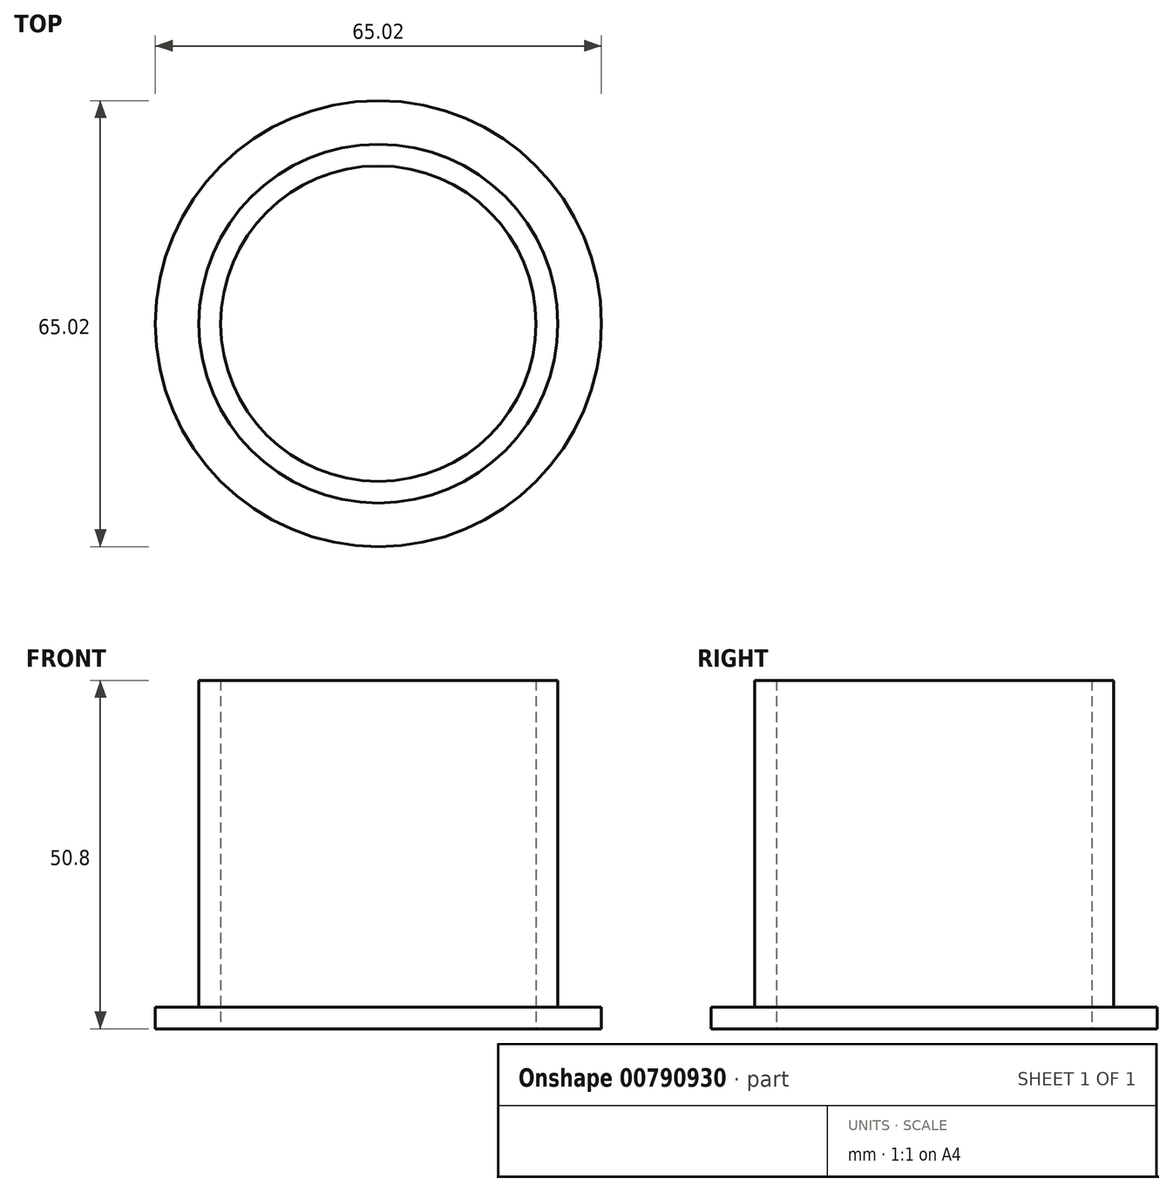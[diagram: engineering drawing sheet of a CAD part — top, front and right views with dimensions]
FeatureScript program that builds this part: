
annotation { "Feature Type Name" : "Feature", "Feature Type Description" : "" }
export const myFeature = defineFeature(function(context is Context, id is Id, definition is map)
    precondition{}
    {
        {
            var Q0;
            Q0=qCreatedBy(makeId("Front.planeOp"),FACE);
            var sketch = newSketch(context, id + "F0", { "sketchPlane" : qUnion([Q0])});
            skLineSegment(sketch, "E0.bottom", {"start": v(-26.16, 50.8) * mm, "end": v(-22.99, 50.8) * mm});
            skLineSegment(sketch, "E0.top", {"start": v(-26.16, 0) * mm, "end": v(-22.99, 0) * mm});
            skLineSegment(sketch, "E0.left", {"start": v(-26.16, 50.8) * mm, "end": v(-26.16, 0) * mm});
            skLineSegment(sketch, "E0.right", {"start": v(-22.99, 50.8) * mm, "end": v(-22.99, 0) * mm});
            skLineSegment(sketch, "E1.bottom", {"start": v(-26.16, 0) * mm, "end": v(-32.51, 0) * mm});
            skLineSegment(sketch, "E1.top", {"start": v(-26.16, 3.17) * mm, "end": v(-32.51, 3.17) * mm});
            skLineSegment(sketch, "E1.left", {"start": v(-26.16, 0) * mm, "end": v(-26.16, 3.17) * mm});
            skLineSegment(sketch, "E1.right", {"start": v(-32.51, 0) * mm, "end": v(-32.51, 3.17) * mm});
            skLineSegment(sketch, "E2", {"start": v(0, 0) * mm, "end": v(0, 50.8) * mm});
            skSolve(sketch);
        }
        {
            var Q0;
            Q0=makeQuery(id+"F0.imprint","IMPRINT",FACE,{"disambiguationData":[TD([[makeQuery(id+"F0.imprint","IMPRINT",EDGE,{"derivedFrom":sQuery(id+"F0.wireOp",EDGE,"E0.bottom")}),-1.0]])]});
            var Q1;
            Q1=makeQuery(id+"F0.imprint","IMPRINT",FACE,{"disambiguationData":[TD([[makeQuery(id+"F0.imprint","IMPRINT",EDGE,{"derivedFrom":sQuery(id+"F0.wireOp",EDGE,"E1.bottom")}),-1.0]])]});
            var Q2;
            Q2=sQuery(id+"F0.wireOp",EDGE,"E2");
            revolve(context, id + "F1", {"surfaceOperationType" : NewSurfaceOperationType.NEW, "entities" : qUnion([Q0, Q1]), "axis" : qUnion([Q2]), "revolveType" : RevolveType.FULL});
        }
    });
